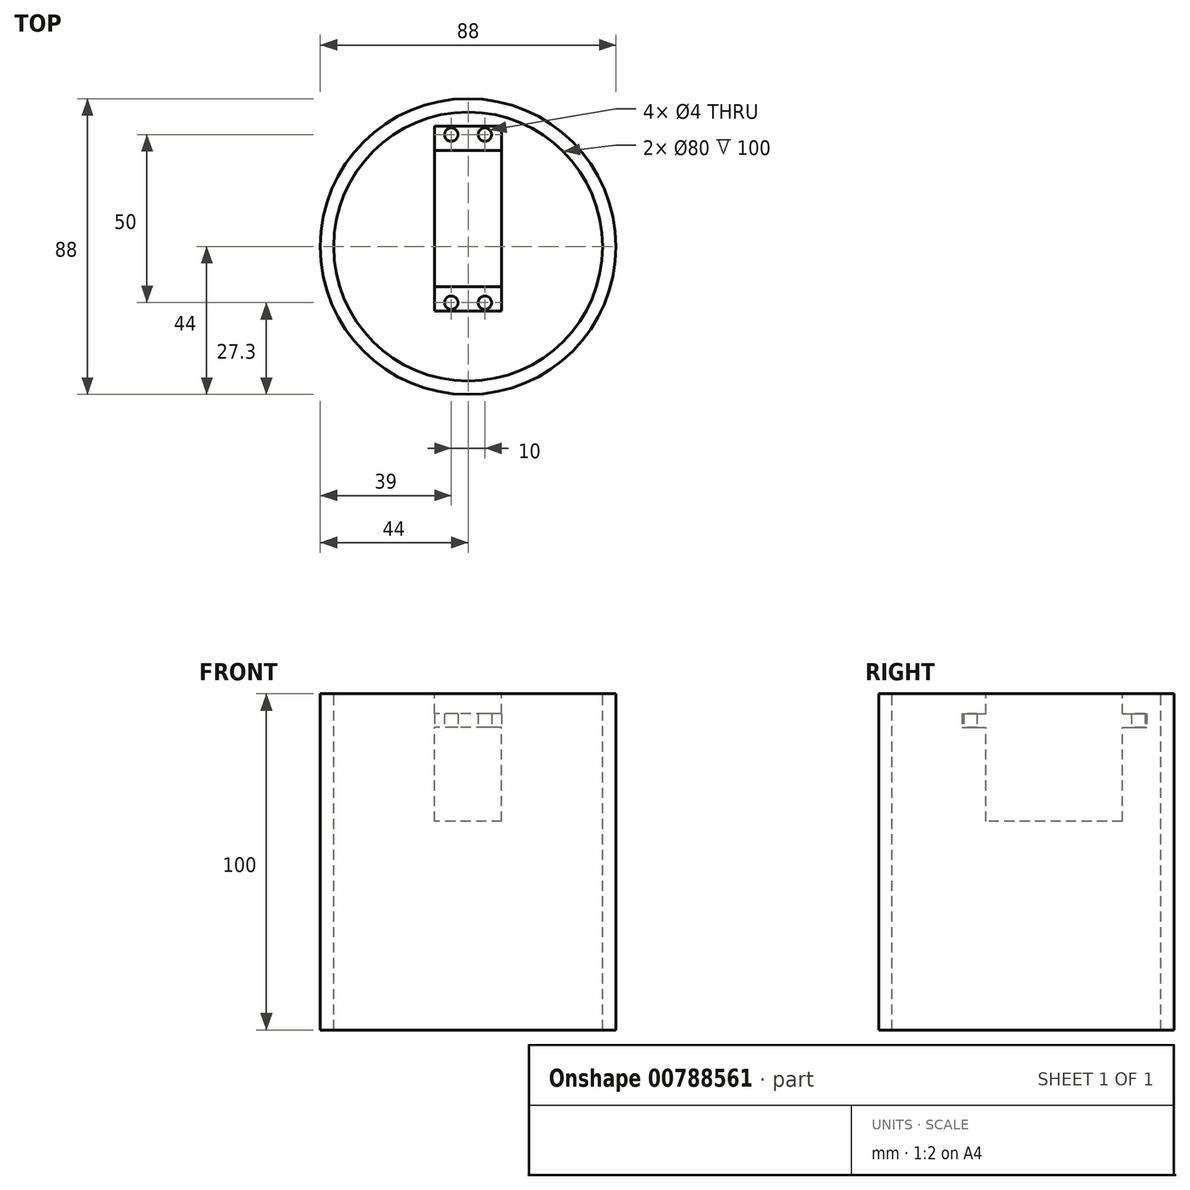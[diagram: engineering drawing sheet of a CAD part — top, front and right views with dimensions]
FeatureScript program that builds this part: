
annotation { "Feature Type Name" : "Feature", "Feature Type Description" : "" }
export const myFeature = defineFeature(function(context is Context, id is Id, definition is map)
    precondition{}
    {
        {
            var Q0;
            Q0=qCreatedBy(makeId("Right.planeOp"),FACE);
            var sketch = newSketch(context, id + "F0", { "sketchPlane" : qUnion([Q0])});
            skLineSegment(sketch, "E0.bottom", {"start": v(20.3, -20.16) * mm, "end": v(-20.3, -20.16) * mm});
            skLineSegment(sketch, "E0.top", {"start": v(20.3, 17.84) * mm, "end": v(-20.3, 17.84) * mm});
            skLineSegment(sketch, "E0.left", {"start": v(20.3, -20.16) * mm, "end": v(20.3, 17.84) * mm});
            skLineSegment(sketch, "E0.right", {"start": v(-20.3, -20.16) * mm, "end": v(-20.3, 17.84) * mm});
            skLineSegment(sketch, "E1.bottom", {"start": v(-27.5, 11.84) * mm, "end": v(27.5, 11.84) * mm});
            skLineSegment(sketch, "E1.top", {"start": v(-27.5, 7.84) * mm, "end": v(27.5, 7.84) * mm});
            skLineSegment(sketch, "E1.left", {"start": v(-27.5, 11.84) * mm, "end": v(-27.5, 7.84) * mm});
            skLineSegment(sketch, "E1.right", {"start": v(27.5, 11.84) * mm, "end": v(27.5, 7.84) * mm});
            skPoint(sketch, "E1.middle", {"position": v(0, 9.84) * mm});
            skSolve(sketch);
        }
        {
            var Q0;
            {var subQ5=sQuery(id+"F0.wireOp",EDGE,"E1.right");Q0=makeQuery(id+"F0.imprint","IMPRINT",FACE,{"disambiguationData":[TD([[makeQuery(id+"F0.imprint","IMPRINT",EDGE,{"derivedFrom":subQ5}),-1.0]])]});}
            var Q1;
            {var subQ0=sQuery(id+"F0.wireOp",EDGE,"E0.top");Q1=makeQuery(id+"F0.imprint","IMPRINT",FACE,{"disambiguationData":[TD([[makeQuery(id+"F0.imprint","IMPRINT",EDGE,{"derivedFrom":subQ0}),1.0]])]});}
            var Q2;
            {var subQ0=sQuery(id+"F0.wireOp",EDGE,"E0.bottom");Q2=makeQuery(id+"F0.imprint","IMPRINT",FACE,{"disambiguationData":[TD([[makeQuery(id+"F0.imprint","IMPRINT",EDGE,{"derivedFrom":subQ0}),-1.0]])]});}
            var Q3;
            {var subQ5=sQuery(id+"F0.wireOp",EDGE,"E1.left");Q3=makeQuery(id+"F0.imprint","IMPRINT",FACE,{"disambiguationData":[TD([[makeQuery(id+"F0.imprint","IMPRINT",EDGE,{"derivedFrom":subQ5}),1.0]])]});}
            var Q4;
            {var subQ0=sQuery(id+"F0.wireOp",EDGE,"E1.top");var subQ1=sQuery(id+"F0.wireOp",EDGE,"E0.left");var subQ2=makeQuery(id+"F0.imprint","INTERSECT",VERTEX,{"derivedFrom":[subQ1,subQ0]});Q4=makeQuery(id+"F0.imprint","IMPRINT",FACE,{"disambiguationData":[TD([[makeQuery(id+"F0.imprint","IMPRINT",EDGE,{"disambiguationData":[TD([[subQ2,-1.0]])],"derivedFrom":subQ1}),1.0]])]});}
            extrude(context, id + "F1", {"entities" : qUnion([Q0, Q1, Q2, Q3, Q4]), "endBound" : BoundingType.SYMMETRIC, "depth" : 20 * mm, "offsetDistance" : 25 * mm});
        }
        {
            var Q0;
            Q0=qCreatedBy(makeId("Top.planeOp"),FACE);
            var sketch = newSketch(context, id + "F2", { "sketchPlane" : qUnion([Q0])});
            skLineSegment(sketch, "E2.bottom", {"start": v(-5, 25) * mm, "end": v(5, 25) * mm, "construction": true});
            skLineSegment(sketch, "E2.top", {"start": v(-5, -25) * mm, "end": v(5, -25) * mm, "construction": true});
            skLineSegment(sketch, "E2.left", {"start": v(-5, 25) * mm, "end": v(-5, -25) * mm, "construction": true});
            skLineSegment(sketch, "E2.right", {"start": v(5, 25) * mm, "end": v(5, -25) * mm, "construction": true});
            skPoint(sketch, "E2.middle", {"position": v(0, 0) * mm});
            skPoint(sketch, "E3", {"position": v(-5, 25) * mm});
            skPoint(sketch, "E4", {"position": v(5, 25) * mm});
            skPoint(sketch, "E5", {"position": v(5, -25) * mm});
            skPoint(sketch, "E6", {"position": v(-5, -25) * mm});
            skCircle(sketch, "E7", {"center": v(-0.1, -8.3) * mm, "radius": 2.5 * mm});
            skSolve(sketch);
        }
        {
            var Q0;
            Q0=makeQuery(id+"F1.opExtrude","SWEPT_FACE",FACE,{"disambiguationData":[OSD([sQuery(id+"F0.wireOp",EDGE,"E0.top")])]});
            var sketch = newSketch(context, id + "F3", { "sketchPlane" : qUnion([Q0])});
            skCircle(sketch, "E8", {"center": v(0, -8.3) * mm, "radius": 44 * mm});
            skCircle(sketch, "E9", {"center": v(0, -8.3) * mm, "radius": 40 * mm});
            skSolve(sketch);
        }
        {
            var Q0;
            Q0=sQuery(id+"F2.wireOp",VERTEX,"E3");
            var Q1;
            Q1=sQuery(id+"F2.wireOp",VERTEX,"E4");
            var Q2;
            Q2=sQuery(id+"F2.wireOp",VERTEX,"E5");
            var Q3;
            Q3=sQuery(id+"F2.wireOp",VERTEX,"E6");
            var Q4;
            Q4=makeQuery(id+"F1.opExtrude","SWEPT_BODY",BODY,{"disambiguationData":[OSD([sQuery(id+"F0.wireOp",EDGE,"E0.bottom"),sQuery(id+"F0.wireOp",EDGE,"E0.top"),sQuery(id+"F0.wireOp",EDGE,"E0.left"),sQuery(id+"F0.wireOp",EDGE,"E0.right"),sQuery(id+"F0.wireOp",EDGE,"E1.bottom"),sQuery(id+"F0.wireOp",EDGE,"E1.top"),sQuery(id+"F0.wireOp",EDGE,"E1.left"),sQuery(id+"F0.wireOp",EDGE,"E1.right")])]});
            hole(context, id + "F4", {"style" : HoleStyle.SIMPLE, "endStyle" : HoleEndStyle.THROUGH, "oppositeDirection" : true, "holeDiameter" : 4 * mm, "majorDiameter" : 5 * mm, "isTappedThrough" : true, "tappedDepth" : 12 * mm, "tapClearance" : 3, "locations" : qUnion([Q0, Q1, Q2, Q3]), "scope" : qUnion([Q4])});
        }
        {
            var Q0;
            Q0=makeQuery(id+"F3.imprint","IMPRINT",FACE,{"disambiguationData":[TD([[makeQuery(id+"F3.imprint","IMPRINT",EDGE,{"derivedFrom":sQuery(id+"F3.wireOp",EDGE,"E8")}),-1.0]])]});
            var Q1;
            Q1=makeQuery(id+"F3.imprint","IMPRINT",FACE,{"disambiguationData":[TD([[makeQuery(id+"F3.imprint","IMPRINT",EDGE,{"derivedFrom":sQuery(id+"F3.wireOp",EDGE,"E8")}),1.0]])]});
            extrude(context, id + "F5", {"entities" : qUnion([Q0, Q1]), "oppositeDirection" : true, "depth" : 100 * mm, "offsetDistance" : 25 * mm});
        }
        {
            var Q0;
            Q0=makeQuery(id+"F3.imprint","IMPRINT",FACE,{"disambiguationData":[TD([[makeQuery(id+"F3.imprint","IMPRINT",EDGE,{"derivedFrom":sQuery(id+"F3.wireOp",EDGE,"E8")}),1.0]])]});
            extrude(context, id + "F6", {"entities" : qUnion([Q0]), "endBound" : BoundingType.UP_TO_NEXT, "oppositeDirection" : true, "depth" : 60 * mm, "offsetDistance" : 25 * mm});
        }
    });
